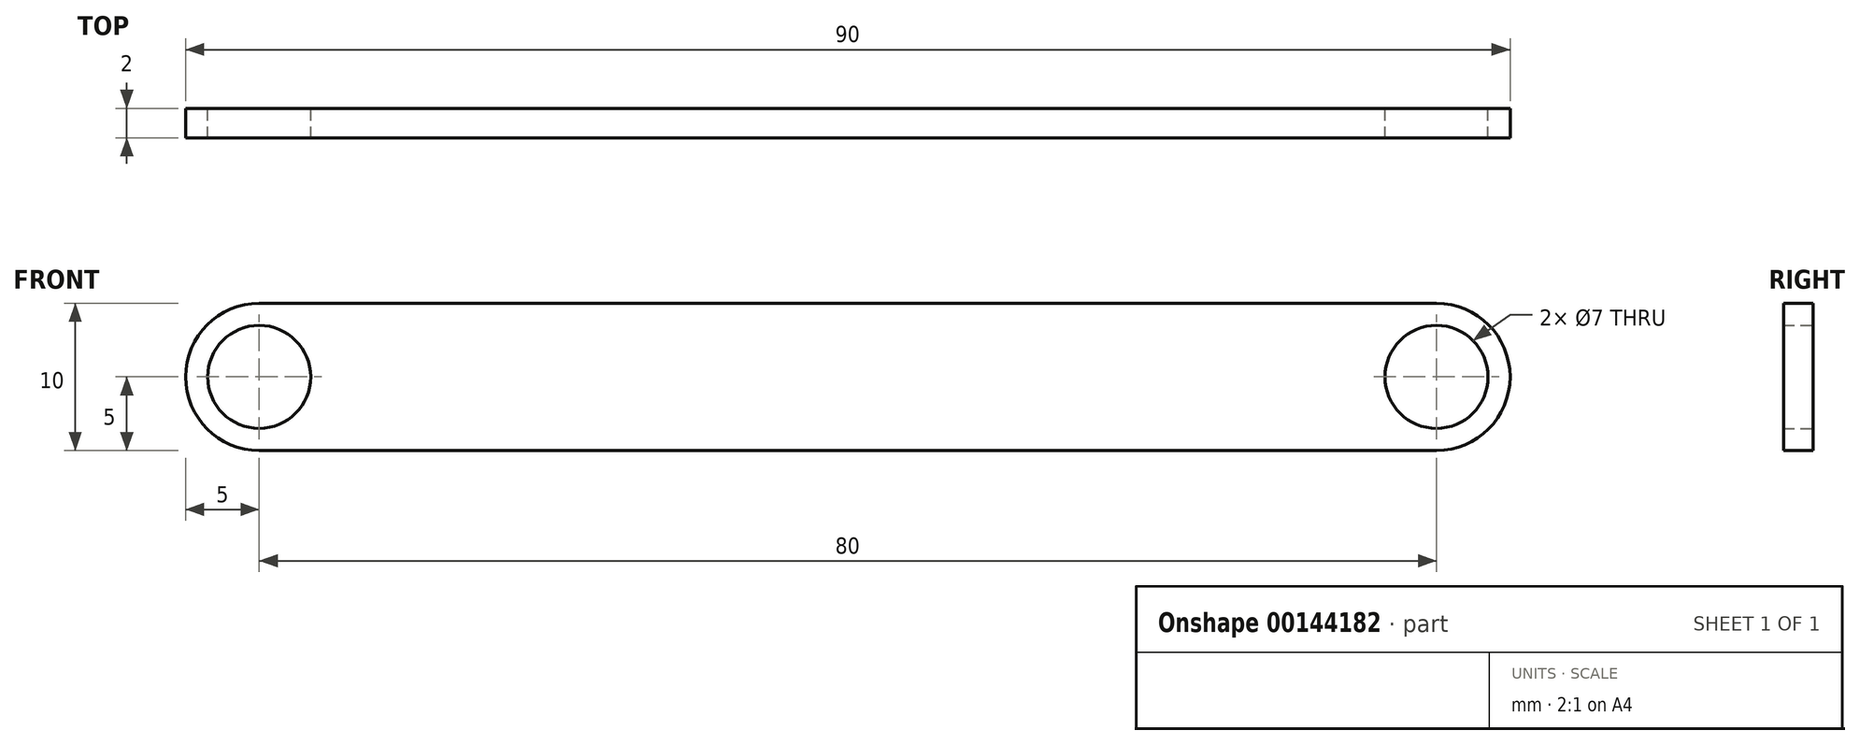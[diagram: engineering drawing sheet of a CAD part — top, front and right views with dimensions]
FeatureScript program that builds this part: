
annotation { "Feature Type Name" : "Feature", "Feature Type Description" : "" }
export const myFeature = defineFeature(function(context is Context, id is Id, definition is map)
    precondition{}
    {
        {
            var Q0;
            Q0=qCreatedBy(makeId("Front.planeOp"),FACE);
            var sketch = newSketch(context, id + "F0", { "sketchPlane" : qUnion([Q0])});
            skLineSegment(sketch, "E0", {"start": v(0, 0) * mm, "end": v(80, 0) * mm});
            skLineSegment(sketch, "E1", {"start": v(0, 10) * mm, "end": v(80, 10) * mm});
            skArc(sketch, "E2", {"start": v(0, 10) * mm, "mid": v(-5, 5) * mm, "end": v(0, 0) * mm});
            skArc(sketch, "E3", {"start": v(80, 0) * mm, "mid": v(85, 5) * mm, "end": v(80, 10) * mm});
            skCircle(sketch, "E4", {"center": v(0, 5) * mm, "radius": 3.5 * mm});
            skCircle(sketch, "E5", {"center": v(80, 5) * mm, "radius": 3.5 * mm});
            skSolve(sketch);
        }
        {
            var Q0;
            Q0=makeQuery(id+"F0.imprint","IMPRINT",FACE,{"disambiguationData":[TD([[makeQuery(id+"F0.imprint","IMPRINT",EDGE,{"derivedFrom":sQuery(id+"F0.wireOp",EDGE,"E0")}),1.0]])]});
            extrude(context, id + "F1", {"entities" : qUnion([Q0]), "depth" : 2 * mm});
        }
    });
